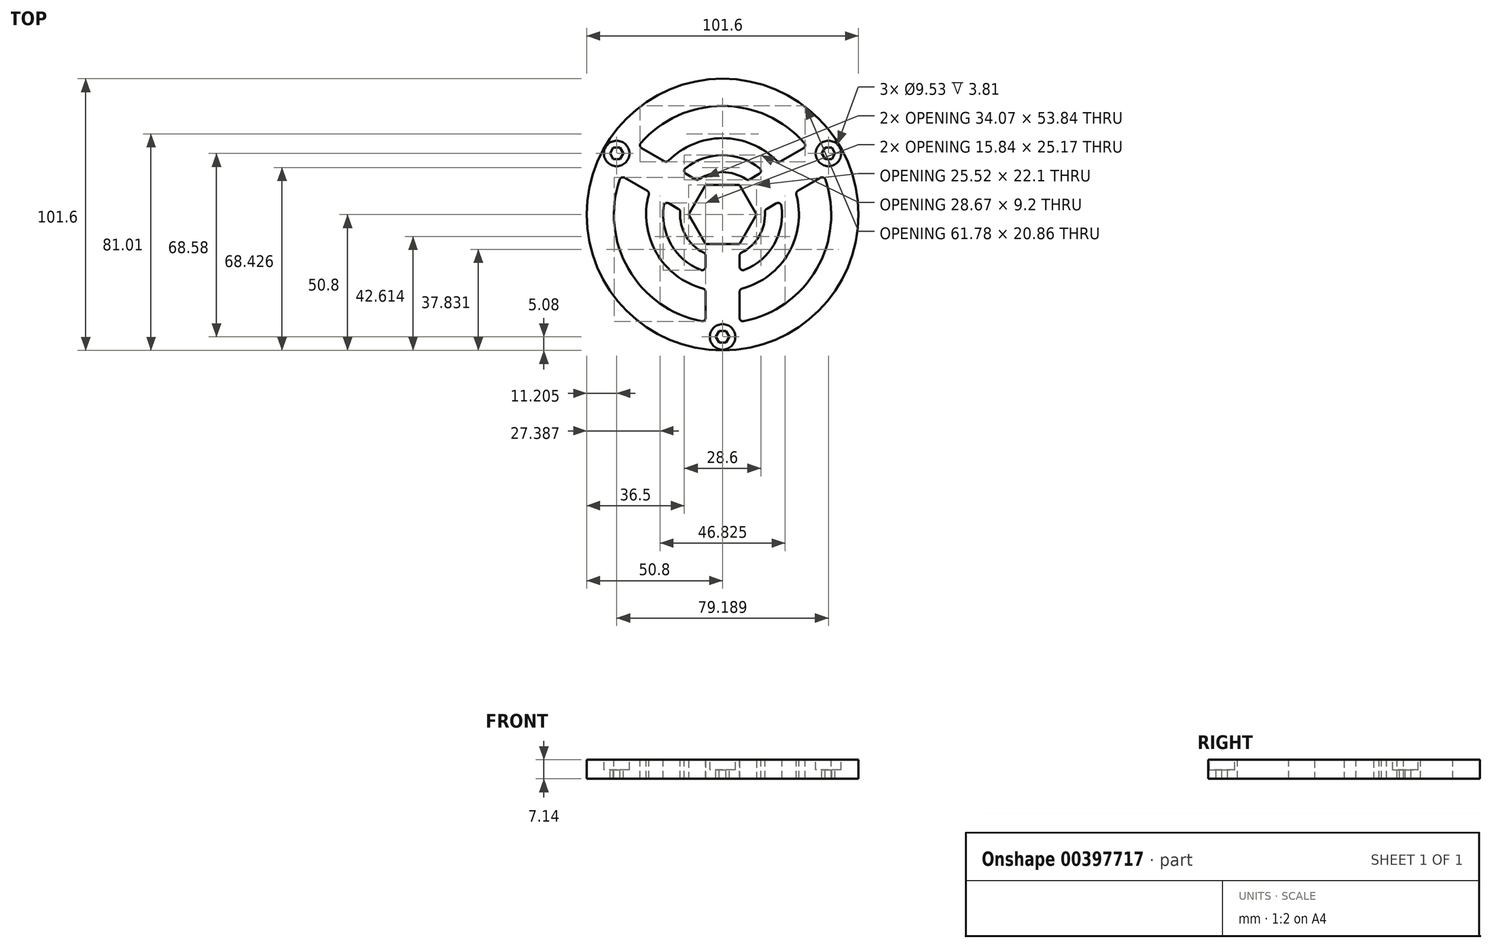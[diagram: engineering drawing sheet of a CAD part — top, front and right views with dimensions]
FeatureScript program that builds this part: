
annotation { "Feature Type Name" : "Feature", "Feature Type Description" : "" }
export const myFeature = defineFeature(function(context is Context, id is Id, definition is map)
    precondition{}
    {
        {
            var Q0;
            Q0=qCreatedBy(makeId("Top.planeOp"),FACE);
            var sketch = newSketch(context, id + "F0", { "sketchPlane" : qUnion([Q0])});
            skCircle(sketch, "E0.cCircle", {"center": v(0, 0) * mm, "radius": 11.05 * mm, "construction": true});
            skLineSegment(sketch, "E0.0", {"start": v(-6.38, 11.05) * mm, "end": v(6.38, 11.05) * mm});
            skLineSegment(sketch, "E0.1", {"start": v(6.38, 11.05) * mm, "end": v(12.76, 0) * mm});
            skLineSegment(sketch, "E0.2", {"start": v(12.76, 0) * mm, "end": v(6.38, -11.05) * mm});
            skLineSegment(sketch, "E0.3", {"start": v(6.38, -11.05) * mm, "end": v(-6.38, -11.05) * mm});
            skLineSegment(sketch, "E0.4", {"start": v(-6.38, -11.05) * mm, "end": v(-12.76, 0) * mm});
            skLineSegment(sketch, "E0.5", {"start": v(-12.76, 0) * mm, "end": v(-6.38, 11.05) * mm});
            skPoint(sketch, "E0.0.midPoint", {"position": v(0, 11.05) * mm});
            skCircle(sketch, "E1", {"center": v(0, 0) * mm, "radius": 50.8 * mm});
            skLineSegment(sketch, "E2", {"start": v(0, 0) * mm, "end": v(0, -45.72) * mm, "construction": true});
            skLineSegment(sketch, "E3", {"start": v(0, 0) * mm, "end": v(41.03, 23.7) * mm, "construction": true});
            skLineSegment(sketch, "E4", {"start": v(0, 0) * mm, "end": v(-40, 23.1) * mm, "construction": true});
            skSolve(sketch);
        }
        {
            var Q0;
            Q0=makeQuery(id+"F0.imprint","IMPRINT",FACE,{"disambiguationData":[TD([[makeQuery(id+"F0.imprint","IMPRINT",EDGE,{"derivedFrom":sQuery(id+"F0.wireOp",EDGE,"E1")}),1.0]])]});
            var Q1;
            Q1=makeQuery(id+"F0.imprint","IMPRINT",FACE,{"disambiguationData":[TD([[makeQuery(id+"F0.imprint","IMPRINT",EDGE,{"derivedFrom":sQuery(id+"F0.wireOp",EDGE,"E0.0")}),1.0]])]});
            extrude(context, id + "F1", {"entities" : qUnion([Q0, Q1]), "depth" : 7.14 * mm});
        }
        {
            var Q0;
            Q0=makeQuery(id+"F1.opExtrude","CAP_FACE",FACE,{"disambiguationData":[OSD([sQuery(id+"F0.wireOp",EDGE,"E0.0"),sQuery(id+"F0.wireOp",EDGE,"E0.1"),sQuery(id+"F0.wireOp",EDGE,"E0.2"),sQuery(id+"F0.wireOp",EDGE,"E0.3"),sQuery(id+"F0.wireOp",EDGE,"E0.4"),sQuery(id+"F0.wireOp",EDGE,"E0.5"),sQuery(id+"F0.wireOp",EDGE,"p1zKd9tD-BlZV-THqY-biXa-5M3YvJ2BDTIW"),sQuery(id+"F0.wireOp",EDGE,"VvwXHANc-y5Kf-Ih7U-FtVy-r8rJaOBLwTHq"),sQuery(id+"F0.wireOp",EDGE,"SWFrPd5f-Phv5-PZbo-TEX7-q7lOXTx6PELk"),sQuery(id+"F0.wireOp",EDGE,"39WtV2oz-ZmbC-Ho3j-i9yz-KZ5qZ733uutH")])],"isStart":false});
            var sketch = newSketch(context, id + "F2", { "sketchPlane" : qUnion([Q0])});
            skCircle(sketch, "E5.cCircle", {"center": v(-39.6, 22.86) * mm, "radius": 2.16 * mm, "construction": true});
            skLineSegment(sketch, "E5.0", {"start": v(-40.84, 25.02) * mm, "end": v(-38.35, 25.02) * mm});
            skLineSegment(sketch, "E5.1", {"start": v(-38.35, 25.02) * mm, "end": v(-37.1, 22.86) * mm});
            skLineSegment(sketch, "E5.2", {"start": v(-37.1, 22.86) * mm, "end": v(-38.35, 20.7) * mm});
            skLineSegment(sketch, "E5.3", {"start": v(-38.35, 20.7) * mm, "end": v(-40.84, 20.7) * mm});
            skLineSegment(sketch, "E5.4", {"start": v(-40.84, 20.7) * mm, "end": v(-42.09, 22.86) * mm});
            skLineSegment(sketch, "E5.5", {"start": v(-42.09, 22.86) * mm, "end": v(-40.84, 25.02) * mm});
            skPoint(sketch, "E5.0.midPoint", {"position": v(-39.6, 25.02) * mm});
            skCircle(sketch, "E6.cCircle", {"center": v(0, -45.72) * mm, "radius": 2.16 * mm, "construction": true});
            skLineSegment(sketch, "E6.0", {"start": v(-1.25, -43.56) * mm, "end": v(1.25, -43.56) * mm});
            skLineSegment(sketch, "E6.1", {"start": v(1.25, -43.56) * mm, "end": v(2.5, -45.72) * mm});
            skLineSegment(sketch, "E6.2", {"start": v(2.5, -45.72) * mm, "end": v(1.25, -47.88) * mm});
            skLineSegment(sketch, "E6.3", {"start": v(1.25, -47.88) * mm, "end": v(-1.25, -47.88) * mm});
            skLineSegment(sketch, "E6.4", {"start": v(-1.25, -47.88) * mm, "end": v(-2.5, -45.72) * mm});
            skLineSegment(sketch, "E6.5", {"start": v(-2.5, -45.72) * mm, "end": v(-1.25, -43.56) * mm});
            skPoint(sketch, "E6.0.midPoint", {"position": v(0, -43.56) * mm});
            skLineSegment(sketch, "E7", {"start": v(0, 0) * mm, "end": v(0, -45.72) * mm, "construction": true});
            skCircle(sketch, "E8.cCircle", {"center": v(39.6, 22.86) * mm, "radius": 2.16 * mm, "construction": true});
            skLineSegment(sketch, "E8.0", {"start": v(38.35, 25.02) * mm, "end": v(40.84, 25.02) * mm});
            skLineSegment(sketch, "E8.1", {"start": v(40.84, 25.02) * mm, "end": v(42.09, 22.86) * mm});
            skLineSegment(sketch, "E8.2", {"start": v(42.09, 22.86) * mm, "end": v(40.84, 20.7) * mm});
            skLineSegment(sketch, "E8.3", {"start": v(40.84, 20.7) * mm, "end": v(38.35, 20.7) * mm});
            skLineSegment(sketch, "E8.4", {"start": v(38.35, 20.7) * mm, "end": v(37.1, 22.86) * mm});
            skLineSegment(sketch, "E8.5", {"start": v(37.1, 22.86) * mm, "end": v(38.35, 25.02) * mm});
            skPoint(sketch, "E8.0.midPoint", {"position": v(39.6, 25.02) * mm});
            skLineSegment(sketch, "E9", {"start": v(-39.6, 22.86) * mm, "end": v(0, 0) * mm, "construction": true});
            skLineSegment(sketch, "E10", {"start": v(0, 0) * mm, "end": v(39.6, 22.86) * mm, "construction": true});
            skArc(sketch, "E11", {"start": v(6.38, -40.14) * mm, "mid": v(35.2, -20.32) * mm, "end": v(37.95, 14.54) * mm});
            skLineSegment(sketch, "E12", {"start": v(-12.76, 0) * mm, "end": v(-37.95, 14.54) * mm});
            skLineSegment(sketch, "E13", {"start": v(-6.38, 11.05) * mm, "end": v(-31.57, 25.6) * mm});
            skLineSegment(sketch, "E14", {"start": v(6.38, 11.05) * mm, "end": v(31.57, 25.6) * mm});
            skLineSegment(sketch, "E15", {"start": v(12.76, 0) * mm, "end": v(37.95, 14.54) * mm});
            skLineSegment(sketch, "E16", {"start": v(6.38, -11.05) * mm, "end": v(6.38, -40.14) * mm});
            skLineSegment(sketch, "E17", {"start": v(-6.38, -11.05) * mm, "end": v(-6.38, -40.14) * mm});
            skArc(sketch, "E18.trimOffspring", {"start": v(31.57, 25.6) * mm, "mid": v(0, 40.64) * mm, "end": v(-31.57, 25.6) * mm});
            skArc(sketch, "E19.trimOffspring", {"start": v(-37.95, 14.54) * mm, "mid": v(-35.2, -20.32) * mm, "end": v(-6.38, -40.14) * mm});
            skCircle(sketch, "E20", {"center": v(0, 0) * mm, "radius": 28.58 * mm});
            skCircle(sketch, "E21", {"center": v(0, 0) * mm, "radius": 22.23 * mm});
            skCircle(sketch, "E22", {"center": v(0, 0) * mm, "radius": 15.88 * mm});
            skSolve(sketch);
        }
        {
            var Q0;
            {var subQ0=sQuery(id+"F2.wireOp",EDGE,"E19.trimOffspring");Q0=makeQuery(id+"F2.imprint","IMPRINT",FACE,{"disambiguationData":[TD([[makeQuery(id+"F2.imprint","IMPRINT",EDGE,{"derivedFrom":subQ0}),1.0]])]});}
            var Q1;
            Q1=makeQuery(id+"F2.imprint","IMPRINT",FACE,{"disambiguationData":[TD([[makeQuery(id+"F2.imprint","IMPRINT",EDGE,{"derivedFrom":sQuery(id+"F2.wireOp",EDGE,"E5.0")}),-1.0]])]});
            var Q2;
            Q2=makeQuery(id+"F2.imprint","IMPRINT",FACE,{"disambiguationData":[TD([[makeQuery(id+"F2.imprint","IMPRINT",EDGE,{"derivedFrom":sQuery(id+"F2.wireOp",EDGE,"E6.0")}),-1.0]])]});
            var Q3;
            Q3=makeQuery(id+"F2.imprint","IMPRINT",FACE,{"disambiguationData":[TD([[makeQuery(id+"F2.imprint","IMPRINT",EDGE,{"derivedFrom":sQuery(id+"F2.wireOp",EDGE,"E8.0")}),-1.0]])]});
            var Q4;
            {var subQ4=sQuery(id+"F2.wireOp",EDGE,"E18.trimOffspring");Q4=makeQuery(id+"F2.imprint","IMPRINT",FACE,{"disambiguationData":[TD([[makeQuery(id+"F2.imprint","IMPRINT",EDGE,{"derivedFrom":subQ4}),1.0]])]});}
            var Q5;
            {var subQ1=sQuery(id+"F2.wireOp",EDGE,"E11");Q5=makeQuery(id+"F2.imprint","IMPRINT",FACE,{"disambiguationData":[TD([[makeQuery(id+"F2.imprint","IMPRINT",EDGE,{"derivedFrom":subQ1}),1.0]])]});}
            var Q6;
            {var subQ0=sQuery(id+"F2.wireOp",EDGE,"E22");var subQ1=sQuery(id+"F2.wireOp",EDGE,"E15");var subQ2=makeQuery(id+"F2.imprint","INTERSECT",VERTEX,{"derivedFrom":[subQ1,subQ0]});Q6=makeQuery(id+"F2.imprint","IMPRINT",FACE,{"disambiguationData":[TD([[makeQuery(id+"F2.imprint","IMPRINT",EDGE,{"disambiguationData":[TD([[subQ2,-1.0]])],"derivedFrom":subQ1}),-1.0]])]});}
            var Q7;
            {var subQ0=sQuery(id+"F2.wireOp",EDGE,"E22");var subQ1=sQuery(id+"F2.wireOp",EDGE,"E13");var subQ2=makeQuery(id+"F2.imprint","INTERSECT",VERTEX,{"derivedFrom":[subQ1,subQ0]});Q7=makeQuery(id+"F2.imprint","IMPRINT",FACE,{"disambiguationData":[TD([[makeQuery(id+"F2.imprint","IMPRINT",EDGE,{"disambiguationData":[TD([[subQ2,-1.0]])],"derivedFrom":subQ1}),-1.0]])]});}
            var Q8;
            {var subQ0=sQuery(id+"F2.wireOp",EDGE,"E22");var subQ1=sQuery(id+"F2.wireOp",EDGE,"E12");var subQ2=makeQuery(id+"F2.imprint","INTERSECT",VERTEX,{"derivedFrom":[subQ1,subQ0]});Q8=makeQuery(id+"F2.imprint","IMPRINT",FACE,{"disambiguationData":[TD([[makeQuery(id+"F2.imprint","IMPRINT",EDGE,{"disambiguationData":[TD([[subQ2,-1.0]])],"derivedFrom":subQ1}),1.0]])]});}
            extrude(context, id + "F3", {"entities" : qUnion([Q0, Q1, Q2, Q3, Q4, Q5, Q6, Q7, Q8]), "operationType" : NewBodyOperationType.REMOVE, "endBound" : BoundingType.THROUGH_ALL, "oppositeDirection" : true, "depth" : 25.4 * mm});
        }
        {
            var Q0;
            Q0=makeQuery(id+"F3.boolean.opBoolean","COPY",EDGE,{"derivedFrom":makeQuery(id+"F3.opExtrude","SWEPT_EDGE",EDGE,{"disambiguationData":[OSD([sQuery(id+"F2.wireOp",EDGE,"E16"),sQuery(id+"F2.wireOp",EDGE,"85d60133-7010-409b-82fa-abbf7276fa56.0")])]})});
            var Q1;
            Q1=makeQuery(id+"F3.boolean.opBoolean","COPY",EDGE,{"derivedFrom":makeQuery(id+"F3.opExtrude","SWEPT_EDGE",EDGE,{"disambiguationData":[OSD([sQuery(id+"F2.wireOp",EDGE,"85d60133-7010-409b-82fa-abbf7276fa56.0"),sQuery(id+"F2.wireOp",EDGE,"85d60133-7010-409b-82fa-abbf7276fa56.5")])]})});
            var Q2;
            Q2=makeQuery(id+"F3.boolean.opBoolean","COPY",EDGE,{"derivedFrom":makeQuery(id+"F3.opExtrude","SWEPT_EDGE",EDGE,{"disambiguationData":[OSD([sQuery(id+"F2.wireOp",EDGE,"85d60133-7010-409b-82fa-abbf7276fa56.4"),sQuery(id+"F2.wireOp",EDGE,"85d60133-7010-409b-82fa-abbf7276fa56.5")])]})});
            var Q3;
            Q3=makeQuery(id+"F3.boolean.opBoolean","COPY",EDGE,{"derivedFrom":makeQuery(id+"F3.opExtrude","SWEPT_EDGE",EDGE,{"disambiguationData":[OSD([sQuery(id+"F2.wireOp",EDGE,"E15"),sQuery(id+"F2.wireOp",EDGE,"85d60133-7010-409b-82fa-abbf7276fa56.4")])]})});
            var Q4;
            Q4=makeQuery(id+"F3.boolean.opBoolean","COPY",EDGE,{"derivedFrom":makeQuery(id+"F3.opExtrude","SWEPT_EDGE",EDGE,{"disambiguationData":[OSD([sQuery(id+"F2.wireOp",EDGE,"E17"),sQuery(id+"F2.wireOp",EDGE,"85d60133-7010-409b-82fa-abbf7276fa56.0")])]})});
            var Q5;
            Q5=makeQuery(id+"F3.boolean.opBoolean","COPY",EDGE,{"derivedFrom":makeQuery(id+"F3.opExtrude","SWEPT_EDGE",EDGE,{"disambiguationData":[OSD([sQuery(id+"F2.wireOp",EDGE,"85d60133-7010-409b-82fa-abbf7276fa56.0"),sQuery(id+"F2.wireOp",EDGE,"85d60133-7010-409b-82fa-abbf7276fa56.3")])]})});
            var Q6;
            Q6=makeQuery(id+"F3.boolean.opBoolean","COPY",EDGE,{"derivedFrom":makeQuery(id+"F3.opExtrude","SWEPT_EDGE",EDGE,{"disambiguationData":[OSD([sQuery(id+"F2.wireOp",EDGE,"85d60133-7010-409b-82fa-abbf7276fa56.1"),sQuery(id+"F2.wireOp",EDGE,"85d60133-7010-409b-82fa-abbf7276fa56.3")])]})});
            var Q7;
            Q7=makeQuery(id+"F3.boolean.opBoolean","COPY",EDGE,{"derivedFrom":makeQuery(id+"F3.opExtrude","SWEPT_EDGE",EDGE,{"disambiguationData":[OSD([sQuery(id+"F2.wireOp",EDGE,"E12"),sQuery(id+"F2.wireOp",EDGE,"85d60133-7010-409b-82fa-abbf7276fa56.1")])]})});
            var Q8;
            Q8=makeQuery(id+"F3.boolean.opBoolean","COPY",EDGE,{"derivedFrom":makeQuery(id+"F3.opExtrude","SWEPT_EDGE",EDGE,{"disambiguationData":[OSD([sQuery(id+"F2.wireOp",EDGE,"E14"),sQuery(id+"F2.wireOp",EDGE,"85d60133-7010-409b-82fa-abbf7276fa56.4")])]})});
            var Q9;
            Q9=makeQuery(id+"F3.boolean.opBoolean","COPY",EDGE,{"derivedFrom":makeQuery(id+"F3.opExtrude","SWEPT_EDGE",EDGE,{"disambiguationData":[OSD([sQuery(id+"F2.wireOp",EDGE,"85d60133-7010-409b-82fa-abbf7276fa56.2"),sQuery(id+"F2.wireOp",EDGE,"85d60133-7010-409b-82fa-abbf7276fa56.4")])]})});
            var Q10;
            Q10=makeQuery(id+"F3.boolean.opBoolean","COPY",EDGE,{"derivedFrom":makeQuery(id+"F3.opExtrude","SWEPT_EDGE",EDGE,{"disambiguationData":[OSD([sQuery(id+"F2.wireOp",EDGE,"85d60133-7010-409b-82fa-abbf7276fa56.1"),sQuery(id+"F2.wireOp",EDGE,"85d60133-7010-409b-82fa-abbf7276fa56.2")])]})});
            var Q11;
            Q11=makeQuery(id+"F3.boolean.opBoolean","COPY",EDGE,{"derivedFrom":makeQuery(id+"F3.opExtrude","SWEPT_EDGE",EDGE,{"disambiguationData":[OSD([sQuery(id+"F2.wireOp",EDGE,"E13"),sQuery(id+"F2.wireOp",EDGE,"85d60133-7010-409b-82fa-abbf7276fa56.1")])]})});
            fillet(context, id + "F4", {"entities" : qUnion([Q0, Q1, Q2, Q3, Q4, Q5, Q6, Q7, Q8, Q9, Q10, Q11]), "radius" : 1.27 * mm, "tangentPropagation" : true, "allowEdgeOverflow" : false});
        }
        {
            var Q0;
            Q0=makeQuery(id+"F1.opExtrude","CAP_FACE",FACE,{"disambiguationData":[OSD([sQuery(id+"F0.wireOp",EDGE,"E0.0"),sQuery(id+"F0.wireOp",EDGE,"E0.1"),sQuery(id+"F0.wireOp",EDGE,"E0.2"),sQuery(id+"F0.wireOp",EDGE,"E0.3"),sQuery(id+"F0.wireOp",EDGE,"E0.4"),sQuery(id+"F0.wireOp",EDGE,"E0.5"),sQuery(id+"F0.wireOp",EDGE,"E1")])],"isStart":false});
            var sketch = newSketch(context, id + "F5", { "sketchPlane" : qUnion([Q0])});
            skPoint(sketch, "E23.0", {"position": v(39.6, 22.86) * mm});
            skPoint(sketch, "E23.1", {"position": v(-39.6, 22.86) * mm});
            skPoint(sketch, "E23.2", {"position": v(0, -45.72) * mm});
            skCircle(sketch, "E24", {"center": v(-39.6, 22.86) * mm, "radius": 4.76 * mm});
            skCircle(sketch, "E25", {"center": v(39.6, 22.86) * mm, "radius": 4.76 * mm});
            skCircle(sketch, "E26", {"center": v(0, -45.72) * mm, "radius": 4.76 * mm});
            skSolve(sketch);
        }
        {
            var Q0;
            Q0=makeQuery(id+"F5.imprint","IMPRINT",FACE,{"disambiguationData":[TD([[makeQuery(id+"F5.imprint","IMPRINT",EDGE,{"derivedFrom":sQuery(id+"F5.wireOp",EDGE,"E24")}),1.0]])]});
            var Q1;
            Q1=makeQuery(id+"F5.imprint","IMPRINT",FACE,{"disambiguationData":[TD([[makeQuery(id+"F5.imprint","IMPRINT",EDGE,{"derivedFrom":sQuery(id+"F5.wireOp",EDGE,"E25")}),1.0]])]});
            var Q2;
            Q2=makeQuery(id+"F5.imprint","IMPRINT",FACE,{"disambiguationData":[TD([[makeQuery(id+"F5.imprint","IMPRINT",EDGE,{"derivedFrom":sQuery(id+"F5.wireOp",EDGE,"E26")}),1.0]])]});
            var Q3;
            Q3=sQuery(id+"F5.wireOp",EDGE,"E24");
            var Q4;
            Q4=sQuery(id+"F5.wireOp",EDGE,"E25");
            var Q5;
            Q5=sQuery(id+"F5.wireOp",EDGE,"E26");
            extrude(context, id + "F6", {"entities" : qUnion([Q0, Q1, Q2]), "operationType" : NewBodyOperationType.REMOVE, "surfaceEntities" : qUnion([Q3, Q4, Q5]), "oppositeDirection" : true, "depth" : 3.8 * mm});
        }
    });
